# Revit family: Haworth_BeHold-Design_SlidingDoorCabinet_TopElement_EU_PRELIMINARY
name_source: partatom
category: Furniture Systems
units: mm (PartAtom-declared; Revit-internal decimal feet)

## family parameters
Always vertical = Yes
Cut with Voids When Loaded = No
OmniClass Number = 23.40.70.14.64.21
OmniClass Title = Systems Furniture
Part Type = Normal
Room Calculation Point = No
Round Connector Dimension = Use Diameter
Shared = No
Work Plane-Based = No

## types (6) — shared parameters
Actual Depth = 43 cm
Assembly Code = E2020200
Custom Size = Yes
Description = Haworth - BeHold Design - Sliding Door Cabinet - Top Element
Glide Finish = Haworth _ Polymer _ Undecided
Manufacturer = Haworth
Max. Height = 151 cm
Max. Width = 160 cm
Min. Height = 39 cm
Min. Width = 80 cm
Model = ESDSDAE
Pull Finish = Haworth _ Polymer _ Undecided
Pull Height = 10 cm
Recessed Handle Thickness Left = 2 cm
Revision Number = 1
Size = Verify Final Dim. w/ Haworth
Trim Finish = Haworth _ Polymer _ Undecided
URL = https://www.haworth.com
URL - Product = https://www.haworth.com
Warranty = http://www.haworth.com
zero-valued in all types: Recessed Handle Thickness Right

## per-type parameters (varying)
| type | 1BH | 2BH | 3BH | 4BH | Actual Height | Actual Width | Door Height | Door Width | End to End Sliding Door Pull | Handle 128 128 Pull | Height | Lock Offset Length | Lock Offset Side | Recessed Handle Pull | Width |
| 80w 1BH | Yes | No | No | No | 39 cm | 80 cm | 35 cm | 38 cm | No | Yes | 39 cm | 20 cm | 33 cm | No | 80 cm |
| 90w 2BH | No | Yes | No | No | 76 cm | 90 cm | 72 cm | 43 cm | No | No | 76 cm | 38 cm | 38 cm | Yes | 90 cm |
| 100w 3BH | No | No | Yes | No | 114 cm | 100 cm | 110 cm | 46 cm | Yes | No | 114 cm | 57 cm | 43 cm | No | 100 cm |
| 120w 4BH | No | No | No | Yes | 151 cm | 120 cm | 147 cm | 58 cm | No | Yes | 151 cm | 75 cm | 53 cm | No | 120 cm |
| 140w 3BH | No | No | Yes | No | 114 cm | 140 cm | 110 cm | 68 cm | No | No | 114 cm | 57 cm | 63 cm | Yes | 140 cm |
| 160w 1BH | Yes | No | No | No | 39 cm | 160 cm | 35 cm | 76 cm | Yes | No | 39 cm | 20 cm | 73 cm | No | 160 cm |

## geometry (parser evidence)
native form markers: Sweep x12
no freeform markers — native parametric forms only
